# Revit family: Gutter-Rectangular-Section
name_source: partatom
category: Detail Items
revit_build: Autodesk Revit Architecture 2012 (Build: 20110210_1515)
units: mm (PartAtom-declared; Revit-internal decimal feet)

## types (8) — shared parameters

## per-type parameters (varying)
| type | Depth | Gutter Height | Keynote | Lip Depth | Lip Height | Overflow (1/2"min) |
| 6" x 6" | 0' - 6" | 0' - 6" | 07 62 00.H38 | 0' - 0 1/2" | 0' - 0 1/2" | 0' - 0 1/2" |
| 6" x 4" | 0' - 6" | 0' - 4" | 07 62 00.H36 | 0' - 0 1/2" | 0' - 0 1/2" | 0' - 0 1/2" |
| 6" x 5" | 0' - 6" | 0' - 5" | 07 62 00.H37 | 0' - 0 1/2" | 0' - 0 1/2" | 0' - 0 1/2" |
| 4" x 5" | 0' - 4" | 0' - 5" | 07 62 00.H35 | 0' - 0 1/2" | 0' - 0 1/2" | 0' - 0 1/2" |
| 4" x 4" | 0' - 4" | 0' - 4" | 07 62 00.H34 | 0' - 0 1/2" | 0' - 0 1/2" | 0' - 0 1/2" |
| 8" x 6" | 0' - 8" | 0' - 6" | 07 62 00.H39 | 0' - 0 3/4" | 0' - 0 3/4" | 0' - 0 1/2" |
| 8" x 8" | 0' - 8" | 0' - 8" | 07 62 00.H40 | 0' - 1" | 0' - 1" | 0' - 0 3/4" |
| 10" x 10" | 0' - 10" | 0' - 10" | 07 62 00.H41 | 0' - 1" | 0' - 1 1/2" | 0' - 1" |
